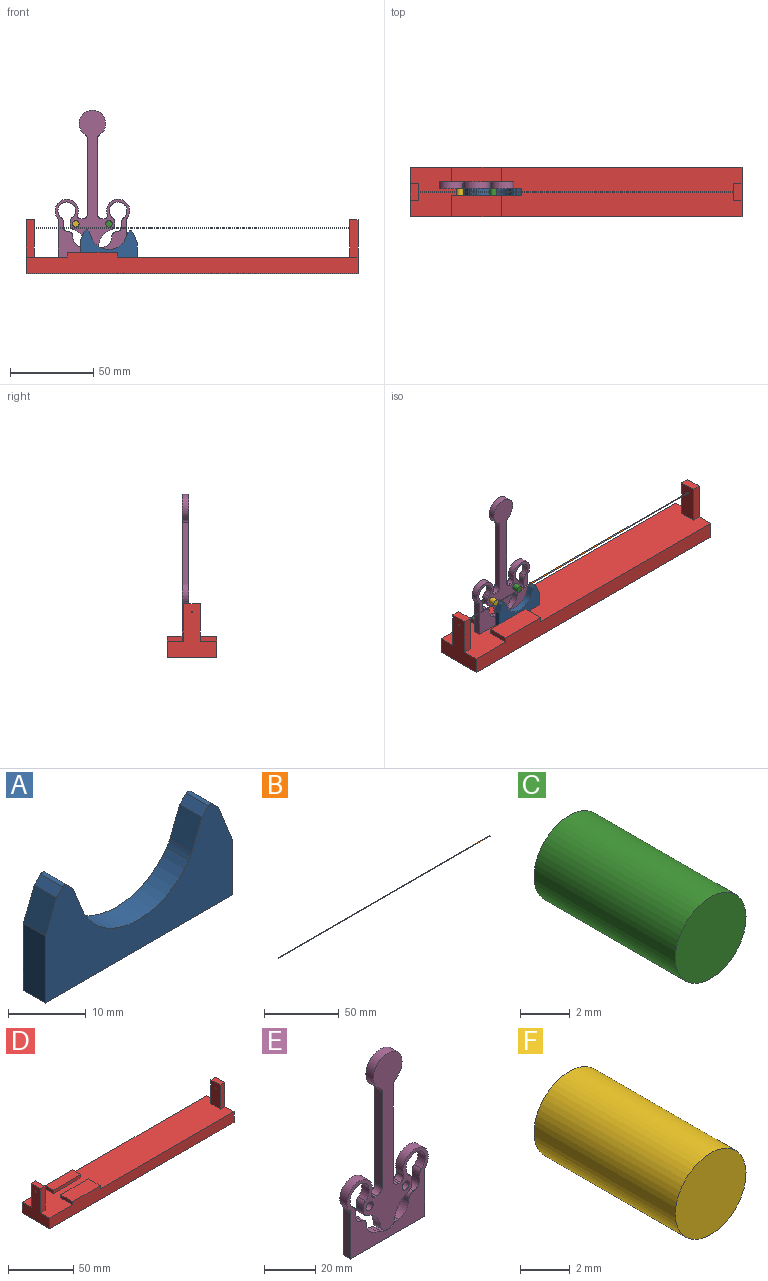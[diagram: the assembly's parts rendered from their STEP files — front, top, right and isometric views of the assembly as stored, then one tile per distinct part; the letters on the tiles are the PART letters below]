
ASSEMBLY  parts=6 mates=5
PART A: 17 faces, bbox 34x4x16.8 mm
  f0: plane 10.5x4mm, normal (-1,0,0), area 42mm2, adj f1,f12,f13,f14
  f1: plane 34x4mm, normal (0,0,-1), area 136mm2, adj f0,f2,f13,f14
  f2: plane 8.5x4mm, normal (1,0,0), area 34mm2, adj f1,f3,f13,f14
  f3: plane 6.5x4mm, normal (0.93,0,0.37), area 28mm2, adj f2,f4,f13,f14
  f4: plane 4x1.15mm, normal (0.71,0,0.71), area 6.5mm2, adj f3,f13,f14,f15
  f5: plane 4x1.15mm, normal (-0.71,0,0.71), area 6.5mm2, adj f6,f13,f14,f15
  f6: plane 4.56x4mm, normal (-0.93,0,0.37), area 19.6mm2, adj f5,f7,f13,f14
  f7: cylinder r=5mm len=4mm, axis (0,1,0), area 4.5mm2, adj f6,f8,f13,f14
  f8: cylinder r=11.18mm len=19.05mm, axis (0,1,0), area 91.4mm2, adj f7,f9,f13,f14
  f9: plane 5x4mm, normal (0.93,0,0.37), area 21.5mm2, adj f8,f10,f13,f14
  f10: plane 4x1.15mm, normal (0.71,0,0.71), area 6.5mm2, adj f9,f13,f14,f16
  f11: plane 4x1.15mm, normal (-0.71,0,0.71), area 6.5mm2, adj f12,f13,f14,f16
  f12: plane 5x4mm, normal (-0.93,0,0.37), area 21.5mm2, adj f0,f11,f13,f14
  f13: plane 34x16.79mm, normal (0,-1,0), area 324.8mm2, adj f0,f1,f2,f3,f4,f5,f6,f7
  f14: plane 34x16.79mm, normal (0,1,0), area 324.8mm2, adj f0,f1,f2,f3,f4,f5,f6,f7
  f15: cylinder r=0.5mm len=4mm, axis (0,1,0), area 3.1mm2, adj f4,f5,f13,f14
  f16: cylinder r=0.5mm len=4mm, axis (0,1,0), area 3.1mm2, adj f10,f11,f13,f14
PART B: 3 faces, bbox 200x0.5x0.5 mm
  f0: cylinder r=0.25mm len=200mm, axis (-1,0,0), area 314.2mm2, adj f1,f2
  f1: plane 0.5x0.5mm, normal (1,0,0), area 0.2mm2, adj f0
  f2: plane 0.5x0.5mm, normal (-1,0,0), area 0.2mm2, adj f0
PART C: 3 faces, bbox 4x8x4 mm
  f0: cylinder r=2mm len=8mm, axis (0,1,0), area 100.5mm2, adj f1,f2
  f1: plane 4x4mm, normal (0,-1,0), area 12.6mm2, adj f0
  f2: plane 4x4mm, normal (0,1,0), area 12.6mm2, adj f0
PART D: 24 faces, bbox 200x30x32.5 mm
  f0: plane 200x30mm, normal (0,0,1), area 5240mm2, adj f1,f2,f3,f4,f6,f7,f8,f10
  f1: plane 32.5x30mm, normal (-1,0,0), area 524.2mm2, adj f0,f2,f4,f5,f10,f11,f13,f14
  f2: plane 200x13mm, normal (0,-1,0), area 2090mm2, adj f0,f1,f3,f5,f21,f22,f23
  f3: plane 32.5x30mm, normal (1,0,0), area 524.2mm2, adj f0,f2,f4,f5,f6,f7,f9,f15
  f4: plane 200x13mm, normal (0,1,0), area 2090mm2, adj f0,f1,f3,f5,f16,f18,f19
  f5: plane 200x30mm, normal (0,0,-1), area 6000mm2, adj f1,f2,f3,f4
  f6: plane 22.5x5mm, normal (0,-1,0), area 112.5mm2, adj f0,f3,f8,f9
  f7: plane 22.5x5mm, normal (0,1,0), area 112.5mm2, adj f0,f3,f8,f9
  f8: plane 22.5x10mm, normal (-1,0,0), area 224.2mm2, adj f0,f6,f7,f9,f15
  f9: plane 10x5mm, normal (0,0,1), area 50mm2, adj f3,f6,f7,f8
  f10: plane 22.5x5mm, normal (0,1,0), area 112.5mm2, adj f0,f1,f12,f13
  f11: plane 22.5x5mm, normal (0,-1,0), area 112.5mm2, adj f0,f1,f12,f13
  f12: plane 22.5x10mm, normal (1,0,0), area 224.2mm2, adj f0,f10,f11,f13,f14
  f13: plane 10x5mm, normal (0,0,1), area 50mm2, adj f1,f10,f11,f12
  f14: cylinder r=0.5mm len=5mm, axis (-1,0,0), area 15.7mm2, adj f1,f12
  f15: cylinder r=0.5mm len=5mm, axis (-1,0,0), area 15.7mm2, adj f3,f8
  f16: plane 9x3mm, normal (-1,0,0), area 27mm2, adj f0,f4,f17,f19
  f17: plane 30x3mm, normal (0,-1,0), area 90mm2, adj f0,f16,f18,f19
  f18: plane 9x3mm, normal (1,0,0), area 27mm2, adj f0,f4,f17,f19
  f19: plane 30x9mm, normal (0,0,1), area 270mm2, adj f4,f16,f17,f18
  f20: plane 30x3mm, normal (0,1,0), area 90mm2, adj f0,f21,f22,f23
  f21: plane 13x3mm, normal (-1,0,0), area 39mm2, adj f0,f2,f20,f23
  f22: plane 13x3mm, normal (1,0,0), area 39mm2, adj f0,f2,f20,f23
  f23: plane 30x13mm, normal (0,0,1), area 390mm2, adj f2,f20,f21,f22
PART E: 48 faces, bbox 45x4x88.4 mm
  f0: cylinder r=1.99mm len=4mm, axis (0,1,0), area 15.1mm2, adj f1,f43,f46,f47
  f1: plane 4x1mm, normal (0,0,1), area 4mm2, adj f0,f2,f46,f47
  f2: cylinder r=3mm len=4mm, axis (0,1,0), area 18.8mm2, adj f1,f3,f46,f47
  f3: plane 45.2x4mm, normal (1,0,0), area 180.8mm2, adj f2,f4,f46,f47
  f4: cylinder r=3mm len=4mm, axis (0,1,0), area 11.9mm2, adj f3,f5,f46,f47
  f5: cylinder r=8mm len=16mm, axis (0,1,0), area 164.1mm2, adj f4,f6,f46,f47
  f6: cylinder r=3mm len=4mm, axis (0,1,0), area 11.9mm2, adj f5,f7,f46,f47
  f7: plane 45.2x4mm, normal (-1,0,0), area 180.8mm2, adj f6,f8,f46,f47
  f8: cylinder r=3mm len=4mm, axis (0,1,0), area 18.8mm2, adj f7,f9,f46,f47
  f9: plane 4x1mm, normal (0,0,1), area 4mm2, adj f8,f10,f46,f47
  f10: cylinder r=1.99mm len=4mm, axis (0,1,0), area 15.1mm2, adj f9,f11,f46,f47
  f11: cylinder r=7mm len=14mm, axis (0,1,0), area 115.2mm2, adj f10,f12,f46,f47
  f12: cylinder r=3mm len=4mm, axis (0,1,0), area 7.7mm2, adj f11,f13,f46,f47
  f13: plane 21.9x4mm, normal (-1,0,0), area 87.6mm2, adj f12,f14,f46,f47
  f14: plane 41x4mm, normal (0,0,-1), area 164mm2, adj f13,f15,f46,f47
  f15: plane 21.9x4mm, normal (1,0,0), area 87.6mm2, adj f14,f16,f46,f47
  f16: cylinder r=3mm len=4mm, axis (0,1,0), area 7.7mm2, adj f15,f43,f46,f47
  f17: cylinder r=10.61mm len=8.85mm, axis (0,1,0), area 48.8mm2, adj f18,f44,f46,f47
  f18: cylinder r=4mm len=7.94mm, axis (0,1,0), area 46.4mm2, adj f17,f19,f46,f47
  f19: cylinder r=10.61mm len=8.85mm, axis (0,1,0), area 48.8mm2, adj f18,f20,f46,f47
  f20: cylinder r=3mm len=4mm, axis (0,1,0), area 15.2mm2, adj f19,f21,f46,f47
  f21: plane 4x2.06mm, normal (1,0,0), area 8.2mm2, adj f20,f22,f46,f47
  f22: cylinder r=3mm len=4mm, axis (0,1,0), area 11.1mm2, adj f21,f23,f46,f47
  f23: cylinder r=5.3mm len=10.6mm, axis (0,1,0), area 105.6mm2, adj f22,f24,f46,f47
  f24: cylinder r=3mm len=4mm, axis (0,1,0), area 11.1mm2, adj f23,f25,f46,f47
  f25: plane 4x3.02mm, normal (-1,0,0), area 12.1mm2, adj f24,f26,f46,f47
  f26: cylinder r=3mm len=4mm, axis (0,1,0), area 19.3mm2, adj f25,f27,f46,f47
  f27: cylinder r=3mm len=4mm, axis (0,1,0), area 17.7mm2, adj f26,f28,f46,f47
  f28: plane 4x1mm, normal (-1,0,0), area 4mm2, adj f27,f29,f46,f47
  f29: cylinder r=7mm len=5.85mm, axis (0,1,0), area 34.1mm2, adj f28,f30,f46,f47
  f30: cylinder r=4.33mm len=4mm, axis (0,1,0), area 8.1mm2, adj f29,f31,f46,f47
  f31: cylinder r=7mm len=8mm, axis (0,1,0), area 34.1mm2, adj f30,f32,f46,f47
  f32: cylinder r=4.33mm len=4mm, axis (0,1,0), area 8.1mm2, adj f31,f33,f46,f47
  f33: cylinder r=7mm len=5.85mm, axis (0,1,0), area 34.1mm2, adj f32,f34,f46,f47
  f34: plane 4x1mm, normal (1,0,0), area 4mm2, adj f33,f35,f46,f47
  f35: cylinder r=3mm len=4mm, axis (0,1,0), area 17.7mm2, adj f34,f36,f46,f47
  f36: cylinder r=3mm len=4mm, axis (0,1,0), area 19.3mm2, adj f35,f37,f46,f47
  f37: plane 4x3.02mm, normal (1,0,0), area 12.1mm2, adj f36,f38,f46,f47
  f38: cylinder r=3mm len=4mm, axis (0,1,0), area 11.1mm2, adj f37,f39,f46,f47
  f39: cylinder r=5.3mm len=10.6mm, axis (0,1,0), area 105.6mm2, adj f38,f40,f46,f47
  f40: cylinder r=3mm len=4mm, axis (0,1,0), area 11.1mm2, adj f39,f41,f46,f47
  f41: plane 4x2.06mm, normal (-1,0,0), area 8.2mm2, adj f40,f44,f46,f47
  f42: cylinder r=2mm len=4mm, axis (0,1,0), area 50.3mm2, adj f46,f47
  f43: cylinder r=7mm len=14mm, axis (0,1,0), area 115.2mm2, adj f0,f16,f46,f47
  f44: cylinder r=3mm len=4mm, axis (0,1,0), area 15.2mm2, adj f17,f41,f46,f47
  f45: cylinder r=2mm len=4mm, axis (0,1,0), area 50.3mm2, adj f46,f47
  f46: plane 88.42x45mm, normal (0,-1,0), area 1348.1mm2, adj f0,f1,f2,f3,f4,f5,f6,f7
  f47: plane 88.42x45mm, normal (0,1,0), area 1348.1mm2, adj f0,f1,f2,f3,f4,f5,f6,f7
PART F: 3 faces, bbox 4x8x4 mm
  f0: cylinder r=2mm len=8mm, axis (0,1,0), area 100.5mm2, adj f1,f2
  f1: plane 4x4mm, normal (0,-1,0), area 12.6mm2, adj f0
  f2: plane 4x4mm, normal (0,1,0), area 12.6mm2, adj f0
PLACE A t=(-56.04,1.36,3.08)mm
PLACE B t=(-106.04,-0.64,20.58)mm
PLACE C t=(-46.04,5.36,23.08)mm
PLACE D t=(-6.04,-0.64,-6.92)mm fixed
PLACE E t=(-66.04,5.36,23.08)mm
PLACE F t=(-86.04,5.36,23.08)mm
MATE fastened D.f0 <-> E.f14  axis (0,0,1) through (-66.04,5.36,3.08)mm
MATE fastened E.f42 <-> F.f0  axis (0,1,0) through (-76.04,5.36,23.08)mm
MATE fastened E.f45 <-> C.f0  axis (0,1,0) through (-56.04,5.36,23.08)mm
MATE fastened B.f0 <-> D.f14  axis (-1,0,0) through (-106.04,-0.64,20.58)mm
MATE fastened A.f1 <-> D.f0  axis (0,0,-1) through (-56.04,-2.64,3.08)mm
